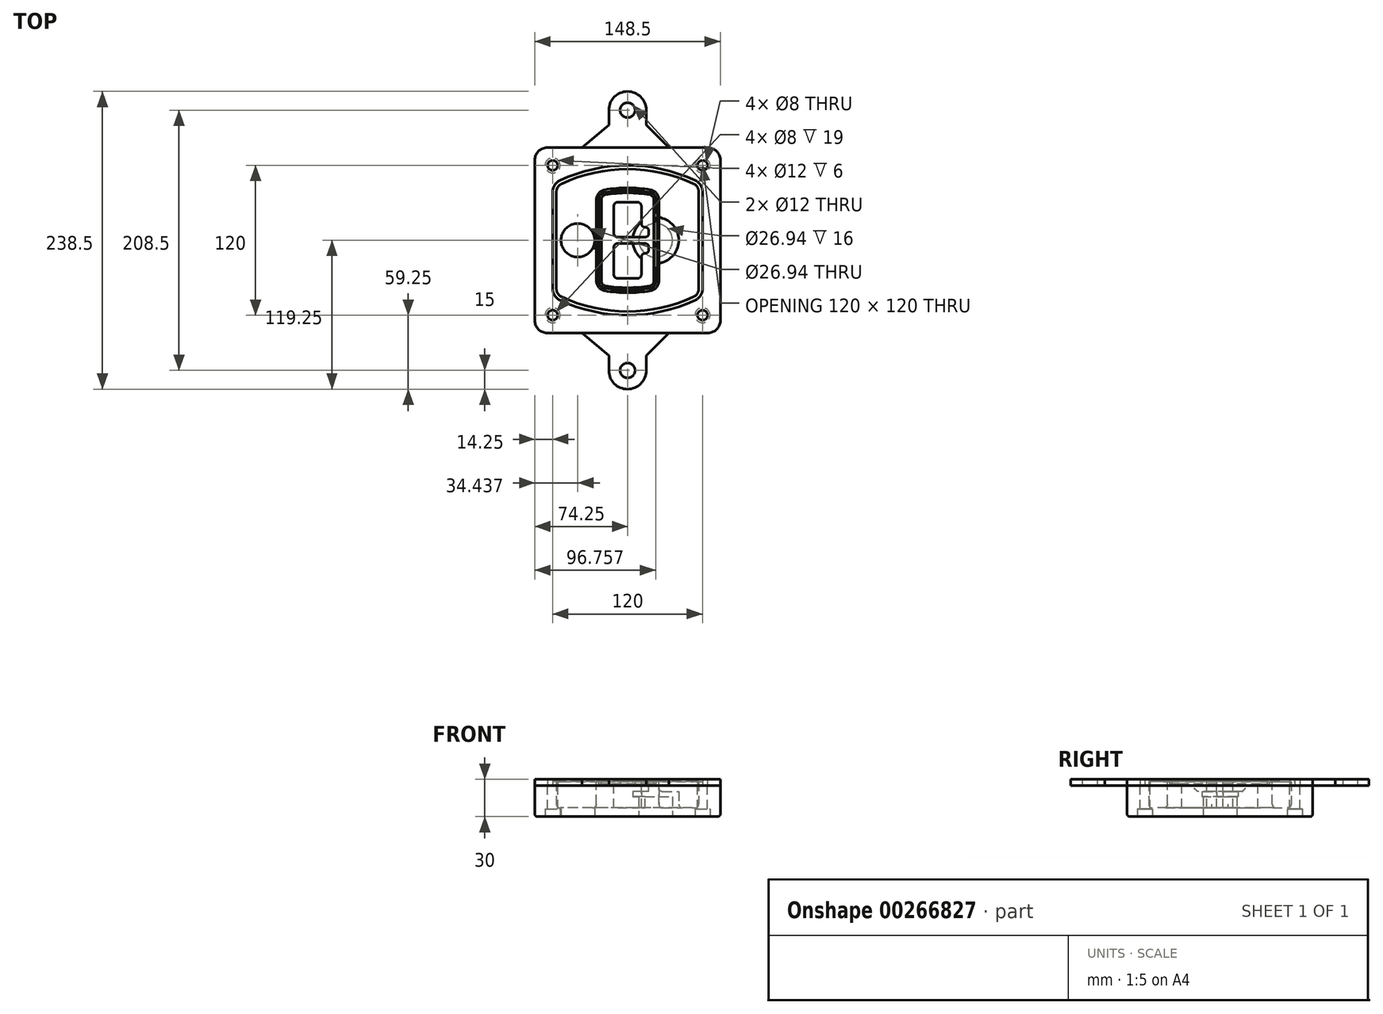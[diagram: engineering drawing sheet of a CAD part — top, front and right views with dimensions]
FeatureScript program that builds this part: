
annotation { "Feature Type Name" : "Feature", "Feature Type Description" : "" }
export const myFeature = defineFeature(function(context is Context, id is Id, definition is map)
    precondition{}
    {
        {
            var Q0;
            Q0=qCreatedBy(makeId("Top.planeOp"),FACE);
            var sketch = newSketch(context, id + "F0", { "sketchPlane" : qUnion([Q0])});
            skPoint(sketch, "E0.rect.middle", {"position": v(0, 0) * mm});
            skLineSegment(sketch, "E1.bottom", {"start": v(-64.25, -74.25) * mm, "end": v(64.25, -74.25) * mm});
            skLineSegment(sketch, "E1.top", {"start": v(-64.25, 74.25) * mm, "end": v(64.25, 74.25) * mm});
            skLineSegment(sketch, "E1.left", {"start": v(-74.25, -64.25) * mm, "end": v(-74.25, 64.25) * mm});
            skLineSegment(sketch, "E1.right", {"start": v(74.25, -64.25) * mm, "end": v(74.25, 64.25) * mm});
            skLineSegment(sketch, "E2", {"start": v(-74.25, 74.25) * mm, "end": v(74.25, -74.25) * mm, "construction": true});
            skLineSegment(sketch, "E3", {"start": v(74.25, 74.25) * mm, "end": v(-74.25, -74.25) * mm, "construction": true});
            skCircle(sketch, "E4", {"center": v(-60, 60) * mm, "radius": 4 * mm});
            skCircle(sketch, "E5", {"center": v(60, 60) * mm, "radius": 4 * mm});
            skCircle(sketch, "E6", {"center": v(60, -60) * mm, "radius": 4 * mm});
            skCircle(sketch, "E7", {"center": v(-60, -60) * mm, "radius": 4 * mm});
            skLineSegment(sketch, "E8", {"start": v(-60, 60) * mm, "end": v(60, 60) * mm, "construction": true});
            skLineSegment(sketch, "E9", {"start": v(60, 60) * mm, "end": v(60, -60) * mm, "construction": true});
            skLineSegment(sketch, "E10", {"start": v(60, -60) * mm, "end": v(-60, -60) * mm, "construction": true});
            skLineSegment(sketch, "E11", {"start": v(-60, -60) * mm, "end": v(-60, 60) * mm, "construction": true});
            skLineSegment(sketch, "E12", {"start": v(-60, 38.83) * mm, "end": v(-60, -38.83) * mm});
            skLineSegment(sketch, "E13", {"start": v(60, 38.83) * mm, "end": v(60, -38.83) * mm});
            skArc(sketch, "E14", {"start": v(54.26, 47.88) * mm, "mid": v(0, 60) * mm, "end": v(-54.26, 47.88) * mm});
            skArc(sketch, "E15", {"start": v(-54.26, -47.88) * mm, "mid": v(0, -60) * mm, "end": v(54.26, -47.88) * mm});
            skLineSegment(sketch, "E16", {"start": v(-60, 0) * mm, "end": v(60, 0) * mm, "construction": true});
            skPoint(sketch, "E17.visualSharp", {"position": v(-60, -45) * mm});
            skArc(sketch, "E17.filletArc", {"start": v(-60, -38.83) * mm, "mid": v(-58.44, -44.2) * mm, "end": v(-54.26, -47.88) * mm});
            skPoint(sketch, "E18.visualSharp", {"position": v(-60, 45) * mm});
            skArc(sketch, "E18.filletArc", {"start": v(-54.26, 47.88) * mm, "mid": v(-58.44, 44.2) * mm, "end": v(-60, 38.83) * mm});
            skPoint(sketch, "E19.visualSharp", {"position": v(60, 45) * mm});
            skArc(sketch, "E19.filletArc", {"start": v(60, 38.83) * mm, "mid": v(58.44, 44.2) * mm, "end": v(54.26, 47.88) * mm});
            skPoint(sketch, "E20.visualSharp", {"position": v(60, -45) * mm});
            skArc(sketch, "E20.filletArc", {"start": v(54.26, -47.88) * mm, "mid": v(58.44, -44.2) * mm, "end": v(60, -38.83) * mm});
            skPoint(sketch, "E21.visualSharp", {"position": v(-74.25, 74.25) * mm});
            skArc(sketch, "E21.filletArc", {"start": v(-64.25, 74.25) * mm, "mid": v(-71.32, 71.32) * mm, "end": v(-74.25, 64.25) * mm});
            skPoint(sketch, "E22.visualSharp", {"position": v(74.25, 74.25) * mm});
            skArc(sketch, "E22.filletArc", {"start": v(74.25, 64.25) * mm, "mid": v(71.32, 71.32) * mm, "end": v(64.25, 74.25) * mm});
            skPoint(sketch, "E23.visualSharp", {"position": v(74.25, -74.25) * mm});
            skArc(sketch, "E23.filletArc", {"start": v(64.25, -74.25) * mm, "mid": v(71.32, -71.32) * mm, "end": v(74.25, -64.25) * mm});
            skPoint(sketch, "E24.visualSharp", {"position": v(-74.25, -74.25) * mm});
            skArc(sketch, "E24.filletArc", {"start": v(-74.25, -64.25) * mm, "mid": v(-71.32, -71.32) * mm, "end": v(-64.25, -74.25) * mm});
            skArc(sketch, "E25.0", {"start": v(57, 38.83) * mm, "mid": v(55.9, 42.58) * mm, "end": v(52.98, 45.17) * mm});
            skLineSegment(sketch, "E25.1", {"start": v(57, 38.83) * mm, "end": v(57, -38.83) * mm});
            skArc(sketch, "E25.2", {"start": v(52.98, -45.17) * mm, "mid": v(55.9, -42.58) * mm, "end": v(57, -38.83) * mm});
            skArc(sketch, "E25.3", {"start": v(-52.98, -45.17) * mm, "mid": v(0, -57) * mm, "end": v(52.98, -45.17) * mm});
            skArc(sketch, "E25.4", {"start": v(-57, -38.83) * mm, "mid": v(-55.9, -42.58) * mm, "end": v(-52.98, -45.17) * mm});
            skArc(sketch, "E25.5", {"start": v(52.98, 45.17) * mm, "mid": v(0, 57) * mm, "end": v(-52.98, 45.17) * mm});
            skLineSegment(sketch, "E25.6", {"start": v(-57, 38.83) * mm, "end": v(-57, -38.83) * mm});
            skArc(sketch, "E25.7", {"start": v(-52.98, 45.17) * mm, "mid": v(-55.9, 42.58) * mm, "end": v(-57, 38.83) * mm});
            skArc(sketch, "E26.0", {"start": v(-55.96, 51.5) * mm, "mid": v(-61.82, 46.33) * mm, "end": v(-64, 38.83) * mm});
            skArc(sketch, "E26.1", {"start": v(55.96, 51.5) * mm, "mid": v(0, 64) * mm, "end": v(-55.96, 51.5) * mm});
            skArc(sketch, "E26.2", {"start": v(64, 38.83) * mm, "mid": v(61.82, 46.33) * mm, "end": v(55.96, 51.5) * mm});
            skLineSegment(sketch, "E26.3", {"start": v(64, 38.83) * mm, "end": v(64, -38.83) * mm});
            skArc(sketch, "E26.4", {"start": v(55.96, -51.5) * mm, "mid": v(61.82, -46.33) * mm, "end": v(64, -38.83) * mm});
            skLineSegment(sketch, "E26.5", {"start": v(-64, 38.83) * mm, "end": v(-64, -38.83) * mm});
            skArc(sketch, "E26.6", {"start": v(-55.96, -51.5) * mm, "mid": v(0, -64) * mm, "end": v(55.96, -51.5) * mm});
            skArc(sketch, "E26.7", {"start": v(-64, -38.83) * mm, "mid": v(-61.82, -46.33) * mm, "end": v(-55.96, -51.5) * mm});
            skSolve(sketch);
        }
        {
            var Q0;
            Q0=makeQuery(id+"F0.imprint","IMPRINT",FACE,{"disambiguationData":[TD([[makeQuery(id+"F0.imprint","IMPRINT",EDGE,{"derivedFrom":sQuery(id+"F0.wireOp",EDGE,"E1.bottom")}),1.0]])]});
            var Q1;
            Q1=makeQuery(id+"F0.imprint","IMPRINT",FACE,{"disambiguationData":[TD([[makeQuery(id+"F0.imprint","IMPRINT",EDGE,{"derivedFrom":sQuery(id+"F0.wireOp",EDGE,"E12")}),1.0]])]});
            var Q2;
            Q2=makeQuery(id+"F0.imprint","IMPRINT",FACE,{"disambiguationData":[TD([[makeQuery(id+"F0.imprint","IMPRINT",EDGE,{"derivedFrom":sQuery(id+"F0.wireOp",EDGE,"E25.0")}),1.0]])]});
            var Q3;
            Q3=makeQuery(id+"F0.imprint","IMPRINT",FACE,{"disambiguationData":[TD([[makeQuery(id+"F0.imprint","IMPRINT",EDGE,{"derivedFrom":sQuery(id+"F0.wireOp",EDGE,"E12")}),-1.0]])]});
            extrude(context, id + "F1", {"entities" : qUnion([Q0, Q1, Q2, Q3]), "oppositeDirection" : true, "depth" : 25 * mm});
        }
        {
            var Q0;
            Q0=makeQuery(id+"F0.imprint","IMPRINT",FACE,{"disambiguationData":[TD([[makeQuery(id+"F0.imprint","IMPRINT",EDGE,{"derivedFrom":sQuery(id+"F0.wireOp",EDGE,"E12")}),1.0]])]});
            extrude(context, id + "F2", {"entities" : qUnion([Q0]), "operationType" : NewBodyOperationType.ADD, "depth" : 3 * mm});
        }
        {
            var Q0;
            Q0=makeQuery(id+"F0.imprint","IMPRINT",FACE,{"disambiguationData":[TD([[makeQuery(id+"F0.imprint","IMPRINT",EDGE,{"derivedFrom":sQuery(id+"F0.wireOp",EDGE,"E25.0")}),1.0]])]});
            extrude(context, id + "F3", {"entities" : qUnion([Q0]), "operationType" : NewBodyOperationType.REMOVE, "oppositeDirection" : true, "depth" : 18 * mm});
        }
        {
            var Q0;
            Q0=makeQuery(id+"F2.opExtrude","CAP_FACE",FACE,{"disambiguationData":[OSD([sQuery(id+"F0.wireOp",EDGE,"E12"),sQuery(id+"F0.wireOp",EDGE,"E13"),sQuery(id+"F0.wireOp",EDGE,"E14"),sQuery(id+"F0.wireOp",EDGE,"E15"),sQuery(id+"F0.wireOp",EDGE,"E17.filletArc"),sQuery(id+"F0.wireOp",EDGE,"E18.filletArc"),sQuery(id+"F0.wireOp",EDGE,"E19.filletArc"),sQuery(id+"F0.wireOp",EDGE,"E20.filletArc"),sQuery(id+"F0.wireOp",EDGE,"E25.0"),sQuery(id+"F0.wireOp",EDGE,"E25.1"),sQuery(id+"F0.wireOp",EDGE,"E25.2"),sQuery(id+"F0.wireOp",EDGE,"E25.3"),sQuery(id+"F0.wireOp",EDGE,"E25.4"),sQuery(id+"F0.wireOp",EDGE,"E25.5"),sQuery(id+"F0.wireOp",EDGE,"E25.6"),sQuery(id+"F0.wireOp",EDGE,"E25.7")])],"isStart":false});
            var sketch = newSketch(context, id + "F4", { "sketchPlane" : qUnion([Q0])});
            skArc(sketch, "E27.0", {"start": v(-18.34, -40.45) * mm, "mid": v(0, -42) * mm, "end": v(18.34, -40.45) * mm});
            skArc(sketch, "E28.0", {"start": v(18.34, 40.45) * mm, "mid": v(0, 42) * mm, "end": v(-18.34, 40.45) * mm});
            skLineSegment(sketch, "E29", {"start": v(-25, 32.57) * mm, "end": v(-25, -32.57) * mm});
            skLineSegment(sketch, "E30", {"start": v(25, 32.57) * mm, "end": v(25, -32.57) * mm});
            skLineSegment(sketch, "E31", {"start": v(-25, 39.1) * mm, "end": v(25, 39.1) * mm, "construction": true});
            skLineSegment(sketch, "E32", {"start": v(-25, -39.1) * mm, "end": v(25, -39.1) * mm, "construction": true});
            skPoint(sketch, "E33.visualSharp", {"position": v(-25, 39.1) * mm});
            skArc(sketch, "E33.filletArc", {"start": v(-18.34, 40.45) * mm, "mid": v(-23.11, 37.73) * mm, "end": v(-25, 32.57) * mm});
            skPoint(sketch, "E34.visualSharp", {"position": v(25, 39.1) * mm});
            skArc(sketch, "E34.filletArc", {"start": v(25, 32.57) * mm, "mid": v(23.11, 37.73) * mm, "end": v(18.34, 40.45) * mm});
            skPoint(sketch, "E35.visualSharp", {"position": v(25, -39.1) * mm});
            skArc(sketch, "E35.filletArc", {"start": v(18.34, -40.45) * mm, "mid": v(23.11, -37.73) * mm, "end": v(25, -32.57) * mm});
            skPoint(sketch, "E36.visualSharp", {"position": v(-25, -39.1) * mm});
            skArc(sketch, "E36.filletArc", {"start": v(-25, -32.57) * mm, "mid": v(-23.11, -37.73) * mm, "end": v(-18.34, -40.45) * mm});
            skArc(sketch, "E37.0", {"start": v(52.98, 45.17) * mm, "mid": v(0, 57) * mm, "end": v(-52.98, 45.17) * mm});
            skArc(sketch, "E37.1", {"start": v(-52.98, 45.17) * mm, "mid": v(-55.9, 42.58) * mm, "end": v(-57, 38.83) * mm});
            skLineSegment(sketch, "E37.2", {"start": v(-57, 38.83) * mm, "end": v(-57, -38.83) * mm});
            skArc(sketch, "E37.3", {"start": v(-57, -38.83) * mm, "mid": v(-55.9, -42.58) * mm, "end": v(-52.98, -45.17) * mm});
            skArc(sketch, "E37.4", {"start": v(-52.98, -45.17) * mm, "mid": v(0, -57) * mm, "end": v(52.98, -45.17) * mm});
            skArc(sketch, "E37.5", {"start": v(52.98, -45.17) * mm, "mid": v(55.9, -42.58) * mm, "end": v(57, -38.83) * mm});
            skLineSegment(sketch, "E37.6", {"start": v(57, 38.83) * mm, "end": v(57, -38.83) * mm});
            skArc(sketch, "E37.7", {"start": v(57, 38.83) * mm, "mid": v(55.9, 42.58) * mm, "end": v(52.98, 45.17) * mm});
            skLineSegment(sketch, "E38.0", {"start": v(23, 32.57) * mm, "end": v(23, -32.57) * mm});
            skArc(sketch, "E38.1", {"start": v(18, -38.48) * mm, "mid": v(21.58, -36.44) * mm, "end": v(23, -32.57) * mm});
            skArc(sketch, "E38.2", {"start": v(-18, -38.48) * mm, "mid": v(0, -40) * mm, "end": v(18, -38.48) * mm});
            skArc(sketch, "E38.3", {"start": v(-23, -32.57) * mm, "mid": v(-21.58, -36.44) * mm, "end": v(-18, -38.48) * mm});
            skLineSegment(sketch, "E38.4", {"start": v(-23, 32.57) * mm, "end": v(-23, -32.57) * mm});
            skArc(sketch, "E38.5", {"start": v(23, 32.57) * mm, "mid": v(21.58, 36.44) * mm, "end": v(18, 38.48) * mm});
            skArc(sketch, "E38.6", {"start": v(-18, 38.48) * mm, "mid": v(-21.58, 36.44) * mm, "end": v(-23, 32.57) * mm});
            skArc(sketch, "E38.7", {"start": v(18, 38.48) * mm, "mid": v(0, 40) * mm, "end": v(-18, 38.48) * mm});
            skArc(sketch, "E39.0", {"start": v(21, 32.57) * mm, "mid": v(20.06, 35.15) * mm, "end": v(17.67, 36.5) * mm});
            skLineSegment(sketch, "E39.1", {"start": v(21, 32.57) * mm, "end": v(21, -32.57) * mm});
            skArc(sketch, "E39.2", {"start": v(17.67, -36.5) * mm, "mid": v(20.06, -35.15) * mm, "end": v(21, -32.57) * mm});
            skArc(sketch, "E39.3", {"start": v(-17.67, -36.5) * mm, "mid": v(0, -38) * mm, "end": v(17.67, -36.5) * mm});
            skArc(sketch, "E39.4", {"start": v(-21, -32.57) * mm, "mid": v(-20.06, -35.15) * mm, "end": v(-17.67, -36.5) * mm});
            skArc(sketch, "E39.5", {"start": v(17.67, 36.5) * mm, "mid": v(0, 38) * mm, "end": v(-17.67, 36.5) * mm});
            skLineSegment(sketch, "E39.6", {"start": v(-21, 32.57) * mm, "end": v(-21, -32.57) * mm});
            skArc(sketch, "E39.7", {"start": v(-17.67, 36.5) * mm, "mid": v(-20.06, 35.15) * mm, "end": v(-21, 32.57) * mm});
            skLineSegment(sketch, "E40", {"start": v(-25, 0) * mm, "end": v(25, 0) * mm, "construction": true});
            skLineSegment(sketch, "E41", {"start": v(-11, 5.5) * mm, "end": v(-11, 27.5) * mm});
            skLineSegment(sketch, "E42", {"start": v(-8, 30.5) * mm, "end": v(8, 30.5) * mm});
            skLineSegment(sketch, "E43", {"start": v(11, 27.5) * mm, "end": v(11, 13.5) * mm});
            skLineSegment(sketch, "E44", {"start": v(14, 10.5) * mm, "end": v(14, 10.5) * mm});
            skLineSegment(sketch, "E45", {"start": v(17, 7.5) * mm, "end": v(17, 5.5) * mm});
            skLineSegment(sketch, "E46", {"start": v(14, 2.5) * mm, "end": v(-8, 2.5) * mm});
            skPoint(sketch, "E47.visualSharp", {"position": v(-11, 30.5) * mm});
            skArc(sketch, "E47.filletArc", {"start": v(-8, 30.5) * mm, "mid": v(-10.12, 29.62) * mm, "end": v(-11, 27.5) * mm});
            skPoint(sketch, "E48.visualSharp", {"position": v(11, 30.5) * mm});
            skArc(sketch, "E48.filletArc", {"start": v(11, 27.5) * mm, "mid": v(10.12, 29.62) * mm, "end": v(8, 30.5) * mm});
            skPoint(sketch, "E49.visualSharp", {"position": v(11, 10.5) * mm});
            skArc(sketch, "E49.filletArc", {"start": v(11, 13.5) * mm, "mid": v(11.88, 11.38) * mm, "end": v(14, 10.5) * mm});
            skPoint(sketch, "E50.visualSharp", {"position": v(17, 10.5) * mm});
            skArc(sketch, "E50.filletArc", {"start": v(17, 7.5) * mm, "mid": v(16.12, 9.62) * mm, "end": v(14, 10.5) * mm});
            skPoint(sketch, "E51.visualSharp", {"position": v(17, 2.5) * mm});
            skArc(sketch, "E51.filletArc", {"start": v(14, 2.5) * mm, "mid": v(16.12, 3.38) * mm, "end": v(17, 5.5) * mm});
            skPoint(sketch, "E52.visualSharp", {"position": v(-11, 2.5) * mm});
            skArc(sketch, "E52.filletArc", {"start": v(-11, 5.5) * mm, "mid": v(-10.12, 3.38) * mm, "end": v(-8, 2.5) * mm});
            skLineSegment(sketch, "E53.0.MirrorCS", {"start": v(14, -2.5) * mm, "end": v(-8, -2.5) * mm});
            skArc(sketch, "E54.0.MirrorCS", {"start": v(-11, -5.5) * mm, "mid": v(-10.12, -3.38) * mm, "end": v(-8, -2.5) * mm});
            skLineSegment(sketch, "E55.0.MirrorCS", {"start": v(-11, -5.5) * mm, "end": v(-11, -27.5) * mm});
            skArc(sketch, "E56.0.MirrorCS", {"start": v(-8, -30.5) * mm, "mid": v(-10.12, -29.62) * mm, "end": v(-11, -27.5) * mm});
            skLineSegment(sketch, "E57.0.MirrorCS", {"start": v(-8, -30.5) * mm, "end": v(8, -30.5) * mm});
            skArc(sketch, "E58.0.MirrorCS", {"start": v(11, -27.5) * mm, "mid": v(10.12, -29.62) * mm, "end": v(8, -30.5) * mm});
            skLineSegment(sketch, "E59.0.MirrorCS", {"start": v(11, -27.5) * mm, "end": v(11, -13.5) * mm});
            skArc(sketch, "E60.0.MirrorCS", {"start": v(11, -13.5) * mm, "mid": v(11.88, -11.38) * mm, "end": v(14, -10.5) * mm});
            skArc(sketch, "E61.0.MirrorCS", {"start": v(17, -7.5) * mm, "mid": v(16.12, -9.62) * mm, "end": v(14, -10.5) * mm});
            skLineSegment(sketch, "E62.0.MirrorCS", {"start": v(17, -7.5) * mm, "end": v(17, -5.5) * mm});
            skArc(sketch, "E63.0.MirrorCS", {"start": v(14, -2.5) * mm, "mid": v(16.12, -3.38) * mm, "end": v(17, -5.5) * mm});
            skSolve(sketch);
        }
        {
            var Q0;
            Q0=makeQuery(id+"F4.imprint","IMPRINT",FACE,{"disambiguationData":[TD([[makeQuery(id+"F4.imprint","IMPRINT",EDGE,{"derivedFrom":sQuery(id+"F4.wireOp",EDGE,"E27.0")}),1.0]])]});
            var Q1;
            Q1=makeQuery(id+"F4.imprint","IMPRINT",FACE,{"disambiguationData":[TD([[makeQuery(id+"F4.imprint","IMPRINT",EDGE,{"derivedFrom":sQuery(id+"F4.wireOp",EDGE,"E38.0")}),-1.0]])]});
            var Q2;
            Q2=makeQuery(id+"F4.imprint","IMPRINT",FACE,{"disambiguationData":[TD([[makeQuery(id+"F4.imprint","IMPRINT",EDGE,{"derivedFrom":sQuery(id+"F4.wireOp",EDGE,"E39.0")}),1.0]])]});
            extrude(context, id + "F5", {"entities" : qUnion([Q0, Q1, Q2]), "operationType" : NewBodyOperationType.ADD, "endBound" : BoundingType.UP_TO_NEXT, "oppositeDirection" : true, "depth" : 25 * mm});
        }
        {
            var Q0;
            Q0=makeQuery(id+"F4.imprint","IMPRINT",FACE,{"disambiguationData":[TD([[makeQuery(id+"F4.imprint","IMPRINT",EDGE,{"derivedFrom":sQuery(id+"F4.wireOp",EDGE,"E38.0")}),-1.0]])]});
            extrude(context, id + "F6", {"entities" : qUnion([Q0]), "operationType" : NewBodyOperationType.REMOVE, "oppositeDirection" : true, "depth" : 2 * mm});
        }
        {
            var Q0;
            Q0=makeQuery(id+"F1.opExtrude","CAP_FACE",FACE,{"disambiguationData":[OSD([sQuery(id+"F0.wireOp",EDGE,"E1.bottom"),sQuery(id+"F0.wireOp",EDGE,"E1.top"),sQuery(id+"F0.wireOp",EDGE,"E1.left"),sQuery(id+"F0.wireOp",EDGE,"E1.right"),sQuery(id+"F0.wireOp",EDGE,"E4"),sQuery(id+"F0.wireOp",EDGE,"E5"),sQuery(id+"F0.wireOp",EDGE,"E6"),sQuery(id+"F0.wireOp",EDGE,"E7"),sQuery(id+"F0.wireOp",EDGE,"E21.filletArc"),sQuery(id+"F0.wireOp",EDGE,"E22.filletArc"),sQuery(id+"F0.wireOp",EDGE,"E23.filletArc"),sQuery(id+"F0.wireOp",EDGE,"E24.filletArc")])],"isStart":false});
            var sketch = newSketch(context, id + "F7", { "sketchPlane" : qUnion([Q0])});
            skCircle(sketch, "E64", {"center": v(22.5, 0) * mm, "radius": 13.47 * mm});
            skCircle(sketch, "E65", {"center": v(-39.81, 0) * mm, "radius": 13.47 * mm});
            skLineSegment(sketch, "E66", {"start": v(74.25, 0) * mm, "end": v(-74.25, 0) * mm});
            skCircle(sketch, "E67", {"center": v(22.5, 0) * mm, "radius": 18.47 * mm});
            skCircle(sketch, "E68", {"center": v(60, -60) * mm, "radius": 6 * mm});
            skCircle(sketch, "E69", {"center": v(-60, -60) * mm, "radius": 6 * mm});
            skCircle(sketch, "E70", {"center": v(-60, 60) * mm, "radius": 6 * mm});
            skCircle(sketch, "E71", {"center": v(60, 60) * mm, "radius": 6 * mm});
            skSolve(sketch);
        }
        {
            var Q0;
            {var subQ1=sQuery(id+"F7.wireOp",EDGE,"E66");var subQ4=sQuery(id+"F7.wireOp",EDGE,"E64");var subQ6=makeQuery(id+"F7.imprint","INTERSECT",VERTEX,{"disambiguationData":[OD(0.0)],"derivedFrom":[subQ4,subQ1]});Q0=makeQuery(id+"F7.imprint","IMPRINT",FACE,{"disambiguationData":[TD([[makeQuery(id+"F7.imprint","IMPRINT",EDGE,{"disambiguationData":[TD([[subQ6,-1.0]])],"derivedFrom":subQ4}),-1.0]])]});}
            var Q1;
            {var subQ0=sQuery(id+"F7.wireOp",EDGE,"E66");var subQ1=sQuery(id+"F7.wireOp",EDGE,"E64");var subQ3=makeQuery(id+"F7.imprint","INTERSECT",VERTEX,{"disambiguationData":[OD(0.0)],"derivedFrom":[subQ1,subQ0]});Q1=makeQuery(id+"F7.imprint","IMPRINT",FACE,{"disambiguationData":[TD([[makeQuery(id+"F7.imprint","IMPRINT",EDGE,{"disambiguationData":[TD([[subQ3,-1.0]])],"derivedFrom":subQ1}),1.0]])]});}
            var Q2;
            {var subQ0=sQuery(id+"F7.wireOp",EDGE,"E66");var subQ1=sQuery(id+"F7.wireOp",EDGE,"E64");var subQ3=makeQuery(id+"F7.imprint","INTERSECT",VERTEX,{"disambiguationData":[OD(0.0)],"derivedFrom":[subQ1,subQ0]});Q2=makeQuery(id+"F7.imprint","IMPRINT",FACE,{"disambiguationData":[TD([[makeQuery(id+"F7.imprint","IMPRINT",EDGE,{"disambiguationData":[TD([[subQ3,1.0]])],"derivedFrom":subQ1}),1.0]])]});}
            var Q3;
            {var subQ1=sQuery(id+"F7.wireOp",EDGE,"E66");var subQ4=sQuery(id+"F7.wireOp",EDGE,"E64");var subQ6=makeQuery(id+"F7.imprint","INTERSECT",VERTEX,{"disambiguationData":[OD(0.0)],"derivedFrom":[subQ4,subQ1]});Q3=makeQuery(id+"F7.imprint","IMPRINT",FACE,{"disambiguationData":[TD([[makeQuery(id+"F7.imprint","IMPRINT",EDGE,{"disambiguationData":[TD([[subQ6,1.0]])],"derivedFrom":subQ4}),-1.0]])]});}
            extrude(context, id + "F8", {"entities" : qUnion([Q0, Q1, Q2, Q3]), "operationType" : NewBodyOperationType.ADD, "oppositeDirection" : true, "depth" : 20 * mm});
        }
        {
            var Q0;
            {var subQ0=sQuery(id+"F7.wireOp",EDGE,"E66");var subQ1=sQuery(id+"F7.wireOp",EDGE,"E64");var subQ3=makeQuery(id+"F7.imprint","INTERSECT",VERTEX,{"disambiguationData":[OD(0.0)],"derivedFrom":[subQ1,subQ0]});Q0=makeQuery(id+"F7.imprint","IMPRINT",FACE,{"disambiguationData":[TD([[makeQuery(id+"F7.imprint","IMPRINT",EDGE,{"disambiguationData":[TD([[subQ3,-1.0]])],"derivedFrom":subQ1}),1.0]])]});}
            var Q1;
            {var subQ0=sQuery(id+"F7.wireOp",EDGE,"E66");var subQ1=sQuery(id+"F7.wireOp",EDGE,"E64");var subQ3=makeQuery(id+"F7.imprint","INTERSECT",VERTEX,{"disambiguationData":[OD(0.0)],"derivedFrom":[subQ1,subQ0]});Q1=makeQuery(id+"F7.imprint","IMPRINT",FACE,{"disambiguationData":[TD([[makeQuery(id+"F7.imprint","IMPRINT",EDGE,{"disambiguationData":[TD([[subQ3,1.0]])],"derivedFrom":subQ1}),1.0]])]});}
            extrude(context, id + "F9", {"entities" : qUnion([Q0, Q1]), "operationType" : NewBodyOperationType.REMOVE, "oppositeDirection" : true, "depth" : 16 * mm});
        }
        {
            var Q0;
            {var subQ0=sQuery(id+"F7.wireOp",EDGE,"E66");var subQ1=sQuery(id+"F7.wireOp",EDGE,"E65");var subQ3=makeQuery(id+"F7.imprint","INTERSECT",VERTEX,{"disambiguationData":[OD(0.0)],"derivedFrom":[subQ1,subQ0]});Q0=makeQuery(id+"F7.imprint","IMPRINT",FACE,{"disambiguationData":[TD([[makeQuery(id+"F7.imprint","IMPRINT",EDGE,{"disambiguationData":[TD([[subQ3,-1.0]])],"derivedFrom":subQ1}),1.0]])]});}
            var Q1;
            {var subQ0=sQuery(id+"F7.wireOp",EDGE,"E66");var subQ1=sQuery(id+"F7.wireOp",EDGE,"E65");var subQ3=makeQuery(id+"F7.imprint","INTERSECT",VERTEX,{"disambiguationData":[OD(0.0)],"derivedFrom":[subQ1,subQ0]});Q1=makeQuery(id+"F7.imprint","IMPRINT",FACE,{"disambiguationData":[TD([[makeQuery(id+"F7.imprint","IMPRINT",EDGE,{"disambiguationData":[TD([[subQ3,1.0]])],"derivedFrom":subQ1}),1.0]])]});}
            extrude(context, id + "F10", {"entities" : qUnion([Q0, Q1]), "operationType" : NewBodyOperationType.REMOVE, "oppositeDirection" : true, "depth" : 25 * mm});
        }
        {
            var Q0;
            Q0=makeQuery(id+"F7.imprint","IMPRINT",FACE,{"disambiguationData":[TD([[makeQuery(id+"F7.imprint","IMPRINT",EDGE,{"derivedFrom":sQuery(id+"F7.wireOp",EDGE,"E68")}),1.0]])]});
            var Q1;
            Q1=makeQuery(id+"F7.imprint","IMPRINT",FACE,{"disambiguationData":[TD([[makeQuery(id+"F7.imprint","IMPRINT",EDGE,{"derivedFrom":makeQuery(id+"F1.opExtrude","CAP_EDGE",EDGE,{"disambiguationData":[OSD([sQuery(id+"F0.wireOp",EDGE,"E5")])],"isStart":false})}),-1.0]])]});
            var Q2;
            Q2=makeQuery(id+"F7.imprint","IMPRINT",FACE,{"disambiguationData":[TD([[makeQuery(id+"F7.imprint","IMPRINT",EDGE,{"derivedFrom":sQuery(id+"F7.wireOp",EDGE,"E69")}),1.0]])]});
            var Q3;
            Q3=makeQuery(id+"F7.imprint","IMPRINT",FACE,{"disambiguationData":[TD([[makeQuery(id+"F7.imprint","IMPRINT",EDGE,{"derivedFrom":makeQuery(id+"F1.opExtrude","CAP_EDGE",EDGE,{"disambiguationData":[OSD([sQuery(id+"F0.wireOp",EDGE,"E4")])],"isStart":false})}),-1.0]])]});
            var Q4;
            Q4=makeQuery(id+"F7.imprint","IMPRINT",FACE,{"disambiguationData":[TD([[makeQuery(id+"F7.imprint","IMPRINT",EDGE,{"derivedFrom":sQuery(id+"F7.wireOp",EDGE,"E70")}),1.0]])]});
            var Q5;
            Q5=makeQuery(id+"F7.imprint","IMPRINT",FACE,{"disambiguationData":[TD([[makeQuery(id+"F7.imprint","IMPRINT",EDGE,{"derivedFrom":makeQuery(id+"F1.opExtrude","CAP_EDGE",EDGE,{"disambiguationData":[OSD([sQuery(id+"F0.wireOp",EDGE,"E7")])],"isStart":false})}),-1.0]])]});
            var Q6;
            Q6=makeQuery(id+"F7.imprint","IMPRINT",FACE,{"disambiguationData":[TD([[makeQuery(id+"F7.imprint","IMPRINT",EDGE,{"derivedFrom":sQuery(id+"F7.wireOp",EDGE,"E71")}),1.0]])]});
            var Q7;
            Q7=makeQuery(id+"F7.imprint","IMPRINT",FACE,{"disambiguationData":[TD([[makeQuery(id+"F7.imprint","IMPRINT",EDGE,{"derivedFrom":makeQuery(id+"F1.opExtrude","CAP_EDGE",EDGE,{"disambiguationData":[OSD([sQuery(id+"F0.wireOp",EDGE,"E6")])],"isStart":false})}),-1.0]])]});
            extrude(context, id + "F11", {"entities" : qUnion([Q0, Q1, Q2, Q3, Q4, Q5, Q6, Q7]), "operationType" : NewBodyOperationType.REMOVE, "oppositeDirection" : true, "depth" : 6 * mm});
        }
        {
            var Q0;
            Q0=makeQuery(id+"F9.boolean.opBoolean","COPY",FACE,{"derivedFrom":makeQuery(id+"F9.opExtrude","CAP_FACE",FACE,{"disambiguationData":[OSD([sQuery(id+"F7.wireOp",EDGE,"E64")])],"isStart":false})});
            var sketch = newSketch(context, id + "F12", { "sketchPlane" : qUnion([Q0])});
            skArc(sketch, "E72.0", {"start": v(11, 14.45) * mm, "mid": v(6.45, 9.13) * mm, "end": v(4.2, 2.5) * mm});
            skArc(sketch, "E72.1", {"start": v(4.2, -2.5) * mm, "mid": v(6.45, -9.13) * mm, "end": v(11, -14.45) * mm});
            skLineSegment(sketch, "E73", {"start": v(4.2, -2.5) * mm, "end": v(14, -2.5) * mm});
            skLineSegment(sketch, "E74.0", {"start": v(14, 2.5) * mm, "end": v(4.2, 2.5) * mm});
            skArc(sketch, "E74.1", {"start": v(14, 2.5) * mm, "mid": v(16.12, 3.38) * mm, "end": v(17, 5.5) * mm});
            skLineSegment(sketch, "E74.2", {"start": v(17, 7.5) * mm, "end": v(17, 5.5) * mm});
            skArc(sketch, "E74.3", {"start": v(17, 7.5) * mm, "mid": v(16.12, 9.62) * mm, "end": v(14, 10.5) * mm});
            skArc(sketch, "E74.4", {"start": v(11, 13.5) * mm, "mid": v(11.88, 11.38) * mm, "end": v(14, 10.5) * mm});
            skLineSegment(sketch, "E74.5", {"start": v(11, 14.45) * mm, "end": v(11, 13.5) * mm});
            skLineSegment(sketch, "E74.7", {"start": v(14, -2.5) * mm, "end": v(4.2, -2.5) * mm});
            skArc(sketch, "E74.8", {"start": v(14, -2.5) * mm, "mid": v(16.12, -3.38) * mm, "end": v(17, -5.5) * mm});
            skLineSegment(sketch, "E74.9", {"start": v(17, -7.5) * mm, "end": v(17, -5.5) * mm});
            skArc(sketch, "E74.10", {"start": v(17, -7.5) * mm, "mid": v(16.12, -9.62) * mm, "end": v(14, -10.5) * mm});
            skArc(sketch, "E74.11", {"start": v(11, -13.5) * mm, "mid": v(11.88, -11.38) * mm, "end": v(14, -10.5) * mm});
            skLineSegment(sketch, "E74.12", {"start": v(11, -14.45) * mm, "end": v(11, -13.5) * mm});
            skPoint(sketch, "E75.orphan", {"position": v(11, -27.5) * mm});
            skPoint(sketch, "E76.orphan", {"position": v(-8, -2.5) * mm});
            skPoint(sketch, "E77.orphan", {"position": v(-8, 2.5) * mm});
            skPoint(sketch, "E78.orphan", {"position": v(11, 27.5) * mm});
            skSolve(sketch);
        }
        {
            var Q0;
            {var subQ7=sQuery(id+"F12.wireOp",EDGE,"E72.0");var subQ14=sQuery(id+"F12.wireOp",EDGE,"E72.1");var subQ16=sQuery(id+"F12.wireOp",EDGE,"E74.1");var subQ18=sQuery(id+"F12.wireOp",EDGE,"E74.8");Q0=qUnion([makeQuery(id+"F12.imprint","IMPRINT",FACE,{"disambiguationData":[TD([[makeQuery(id+"F12.imprint","IMPRINT",EDGE,{"derivedFrom":subQ7}),1.0]])]}),makeQuery(id+"F12.imprint","IMPRINT",FACE,{"disambiguationData":[TD([[makeQuery(id+"F12.imprint","IMPRINT",EDGE,{"derivedFrom":subQ14}),1.0]])]}),makeQuery(id+"F12.imprint","IMPRINT",FACE,{"disambiguationData":[TD([[makeQuery(id+"F12.imprint","IMPRINT",EDGE,{"derivedFrom":subQ16}),1.0]])]}),makeQuery(id+"F12.imprint","IMPRINT",FACE,{"disambiguationData":[TD([[makeQuery(id+"F12.imprint","IMPRINT",EDGE,{"derivedFrom":subQ18}),-1.0]])]})]);}
            var Q1;
            Q1=makeQuery(id+"F5.boolean.opBoolean","SPLIT",FACE,{"disambiguationData":[TD([makeQuery(id+"F5.opExtrude","SWEPT_FACE",FACE,{"disambiguationData":[OSD([sQuery(id+"F4.wireOp",EDGE,"E41")])]})])],"derivedFrom":makeQuery(id+"F3.boolean.opBoolean","COPY",FACE,{"derivedFrom":makeQuery(id+"F3.opExtrude","CAP_FACE",FACE,{"disambiguationData":[OSD([sQuery(id+"F0.wireOp",EDGE,"E25.0"),sQuery(id+"F0.wireOp",EDGE,"E25.1"),sQuery(id+"F0.wireOp",EDGE,"E25.2"),sQuery(id+"F0.wireOp",EDGE,"E25.3"),sQuery(id+"F0.wireOp",EDGE,"E25.4"),sQuery(id+"F0.wireOp",EDGE,"E25.5"),sQuery(id+"F0.wireOp",EDGE,"E25.6"),sQuery(id+"F0.wireOp",EDGE,"E25.7")])],"isStart":false})})});
            extrude(context, id + "F13", {"entities" : qUnion([Q0]), "operationType" : NewBodyOperationType.REMOVE, "endBound" : BoundingType.UP_TO_SURFACE, "endBoundEntityFace" : qUnion([Q1]), "depth" : 25 * mm});
        }
        {
            var Q0;
            Q0=makeQuery(id+"F3.boolean.opBoolean","COPY",EDGE,{"derivedFrom":makeQuery(id+"F3.opExtrude","CAP_EDGE",EDGE,{"disambiguationData":[OSD([sQuery(id+"F0.wireOp",EDGE,"E25.6")])],"isStart":false})});
            var Q1;
            Q1=makeQuery(id+"F8.boolean.opBoolean","INTERSECT",EDGE,{"derivedFrom":[makeQuery(id+"F5.opExtrude","SWEPT_FACE",FACE,{"disambiguationData":[OSD([sQuery(id+"F4.wireOp",EDGE,"E30")])]}),makeQuery(id+"F8.opExtrude","CAP_FACE",FACE,{"disambiguationData":[OSD([sQuery(id+"F7.wireOp",EDGE,"E67")])],"isStart":false})]});
            var Q2;
            Q2=makeQuery(id+"F8.boolean.opBoolean","INTERSECT",EDGE,{"disambiguationData":[OD(1.0)],"derivedFrom":[makeQuery(id+"F5.opExtrude","SWEPT_FACE",FACE,{"disambiguationData":[OSD([sQuery(id+"F4.wireOp",EDGE,"E30")])]}),makeQuery(id+"F8.opExtrude","SWEPT_FACE",FACE,{"disambiguationData":[OSD([sQuery(id+"F7.wireOp",EDGE,"E67")])]})]});
            var Q3;
            {var subQ0=sQuery(id+"F4.wireOp",EDGE,"E30");Q3=makeQuery(id+"F8.boolean.opBoolean","SPLIT",EDGE,{"disambiguationData":[TD([makeQuery(id+"F5.opExtrude","SWEPT_FACE",FACE,{"disambiguationData":[OSD([sQuery(id+"F4.wireOp",EDGE,"E35.filletArc")])]})])],"derivedFrom":makeQuery(id+"F5.opExtrude","CAP_EDGE",EDGE,{"disambiguationData":[OSD([subQ0])],"isStart":false})});}
            var Q4;
            {var subQ0=sQuery(id+"F0.wireOp",EDGE,"E25.7");var subQ1=sQuery(id+"F0.wireOp",EDGE,"E25.1");var subQ2=sQuery(id+"F0.wireOp",EDGE,"E25.6");var subQ3=sQuery(id+"F0.wireOp",EDGE,"E25.5");var subQ4=sQuery(id+"F0.wireOp",EDGE,"E25.4");var subQ5=sQuery(id+"F0.wireOp",EDGE,"E25.0");var subQ6=sQuery(id+"F0.wireOp",EDGE,"E25.2");var subQ7=sQuery(id+"F0.wireOp",EDGE,"E25.3");Q4=makeQuery(id+"F8.boolean.opBoolean","INTERSECT",EDGE,{"derivedFrom":[makeQuery(id+"F5.boolean.opBoolean","SPLIT",FACE,{"disambiguationData":[TD([makeQuery(id+"F2.opExtrude","SWEPT_FACE",FACE,{"disambiguationData":[OSD([subQ5])]})])],"derivedFrom":makeQuery(id+"F3.boolean.opBoolean","COPY",FACE,{"derivedFrom":makeQuery(id+"F3.opExtrude","CAP_FACE",FACE,{"disambiguationData":[OSD([subQ5,subQ1,subQ6,subQ7,subQ4,subQ3,subQ2,subQ0])],"isStart":false})})}),makeQuery(id+"F8.opExtrude","SWEPT_FACE",FACE,{"disambiguationData":[OSD([sQuery(id+"F7.wireOp",EDGE,"E67")])]})]});}
            var Q5;
            Q5=makeQuery(id+"F8.boolean.opBoolean","INTERSECT",EDGE,{"disambiguationData":[OD(0.0)],"derivedFrom":[makeQuery(id+"F5.opExtrude","SWEPT_FACE",FACE,{"disambiguationData":[OSD([sQuery(id+"F4.wireOp",EDGE,"E30")])]}),makeQuery(id+"F8.opExtrude","SWEPT_FACE",FACE,{"disambiguationData":[OSD([sQuery(id+"F7.wireOp",EDGE,"E67")])]})]});
            fillet(context, id + "F14", {"entities" : qUnion([Q0, Q1, Q2, Q3, Q4, Q5]), "radius" : 3 * mm, "tangentPropagation" : true, "allowEdgeOverflow" : false});
        }
        {
            var Q0;
            Q0=makeQuery(id+"F1.opExtrude","CAP_EDGE",EDGE,{"disambiguationData":[OSD([sQuery(id+"F0.wireOp",EDGE,"E1.bottom")])],"isStart":false});
            fillet(context, id + "F15", {"entities" : qUnion([Q0]), "radius" : 2 * mm, "tangentPropagation" : true, "allowEdgeOverflow" : false});
        }
        {
            var Q0;
            {var subQ0=sQuery(id+"F0.wireOp",EDGE,"E22.filletArc");var subQ1=sQuery(id+"F0.wireOp",EDGE,"E7");var subQ2=sQuery(id+"F0.wireOp",EDGE,"E6");var subQ3=sQuery(id+"F0.wireOp",EDGE,"E5");var subQ4=sQuery(id+"F0.wireOp",EDGE,"E4");var subQ5=sQuery(id+"F0.wireOp",EDGE,"E1.bottom");var subQ6=sQuery(id+"F0.wireOp",EDGE,"E21.filletArc");var subQ7=sQuery(id+"F0.wireOp",EDGE,"E1.top");var subQ8=sQuery(id+"F0.wireOp",EDGE,"E1.left");var subQ9=sQuery(id+"F0.wireOp",EDGE,"E1.right");var subQ10=sQuery(id+"F0.wireOp",EDGE,"E23.filletArc");var subQ11=sQuery(id+"F0.wireOp",EDGE,"E24.filletArc");Q0=makeQuery(id+"F2.boolean.opBoolean","SPLIT",FACE,{"disambiguationData":[TD([makeQuery(id+"F1.opExtrude","SWEPT_FACE",FACE,{"disambiguationData":[OSD([subQ5])]})])],"derivedFrom":makeQuery(id+"F1.opExtrude","CAP_FACE",FACE,{"disambiguationData":[OSD([subQ5,subQ7,subQ8,subQ9,subQ4,subQ3,subQ2,subQ1,subQ6,subQ0,subQ10,subQ11])],"isStart":true})});}
            var sketch = newSketch(context, id + "F16", { "sketchPlane" : qUnion([Q0])});
            skLineSegment(sketch, "E79", {"start": v(0, 74.25) * mm, "end": v(0, 104.25) * mm, "construction": true});
            skCircle(sketch, "E80", {"center": v(0, 104.25) * mm, "radius": 6 * mm});
            skArc(sketch, "E81", {"start": v(15, 104.25) * mm, "mid": v(0, 119.25) * mm, "end": v(-15, 104.25) * mm});
            skLineSegment(sketch, "E82", {"start": v(15, 104.25) * mm, "end": v(15, 92.25) * mm});
            skLineSegment(sketch, "E83", {"start": v(15, 92.25) * mm, "end": v(33, 74.25) * mm});
            skLineSegment(sketch, "E84", {"start": v(-36.6, 74.25) * mm, "end": v(-15, 92.25) * mm});
            skLineSegment(sketch, "E85", {"start": v(-15, 104.25) * mm, "end": v(-15, 92.25) * mm});
            skLineSegment(sketch, "E86", {"start": v(-74.25, 0) * mm, "end": v(74.25, 0) * mm, "construction": true});
            skLineSegment(sketch, "E87.MirrorCS", {"start": v(-15, -104.25) * mm, "end": v(-15, -92.25) * mm});
            skLineSegment(sketch, "E88.MirrorCS", {"start": v(15, -104.25) * mm, "end": v(15, -92.25) * mm});
            skCircle(sketch, "E89.MirrorC", {"center": v(0, -104.25) * mm, "radius": 6 * mm});
            skLineSegment(sketch, "E90.MirrorCS", {"start": v(0, -74.25) * mm, "end": v(0, -104.25) * mm, "construction": true});
            skLineSegment(sketch, "E91.MirrorCS", {"start": v(15, -92.25) * mm, "end": v(33, -74.25) * mm});
            skLineSegment(sketch, "E92.MirrorCS", {"start": v(-36.6, -74.25) * mm, "end": v(-15, -92.25) * mm});
            skArc(sketch, "E93.MirrorCS", {"start": v(15, -104.25) * mm, "mid": v(0, -119.25) * mm, "end": v(-15, -104.25) * mm});
            skSolve(sketch);
        }
        {
            var Q0;
            Q0=makeQuery(id+"F16.imprint","IMPRINT",FACE,{"disambiguationData":[TD([[makeQuery(id+"F16.imprint","IMPRINT",EDGE,{"derivedFrom":sQuery(id+"F16.wireOp",EDGE,"E81")}),1.0]])]});
            var Q1;
            Q1=makeQuery(id+"F16.imprint","IMPRINT",FACE,{"disambiguationData":[TD([[makeQuery(id+"F16.imprint","IMPRINT",EDGE,{"derivedFrom":sQuery(id+"F16.wireOp",EDGE,"E87.MirrorCS")}),-1.0]])]});
            extrude(context, id + "F17", {"entities" : qUnion([Q0, Q1]), "depth" : 5 * mm});
        }
        {
            var Q0;
            {var subQ0=sQuery(id+"F0.wireOp",EDGE,"E22.filletArc");var subQ1=sQuery(id+"F0.wireOp",EDGE,"E7");var subQ2=sQuery(id+"F0.wireOp",EDGE,"E6");var subQ3=sQuery(id+"F0.wireOp",EDGE,"E5");var subQ4=sQuery(id+"F0.wireOp",EDGE,"E4");var subQ5=sQuery(id+"F0.wireOp",EDGE,"E1.bottom");var subQ6=sQuery(id+"F0.wireOp",EDGE,"E21.filletArc");var subQ7=sQuery(id+"F0.wireOp",EDGE,"E1.top");var subQ8=sQuery(id+"F0.wireOp",EDGE,"E1.left");var subQ9=sQuery(id+"F0.wireOp",EDGE,"E1.right");var subQ10=sQuery(id+"F0.wireOp",EDGE,"E23.filletArc");var subQ11=sQuery(id+"F0.wireOp",EDGE,"E24.filletArc");Q0=makeQuery(id+"F2.boolean.opBoolean","SPLIT",FACE,{"disambiguationData":[TD([makeQuery(id+"F1.opExtrude","SWEPT_FACE",FACE,{"disambiguationData":[OSD([subQ5])]})])],"derivedFrom":makeQuery(id+"F1.opExtrude","CAP_FACE",FACE,{"disambiguationData":[OSD([subQ5,subQ7,subQ8,subQ9,subQ4,subQ3,subQ2,subQ1,subQ6,subQ0,subQ10,subQ11])],"isStart":true})});}
            extrude(context, id + "F18", {"entities" : qUnion([Q0]), "depth" : 5 * mm});
        }
    });
